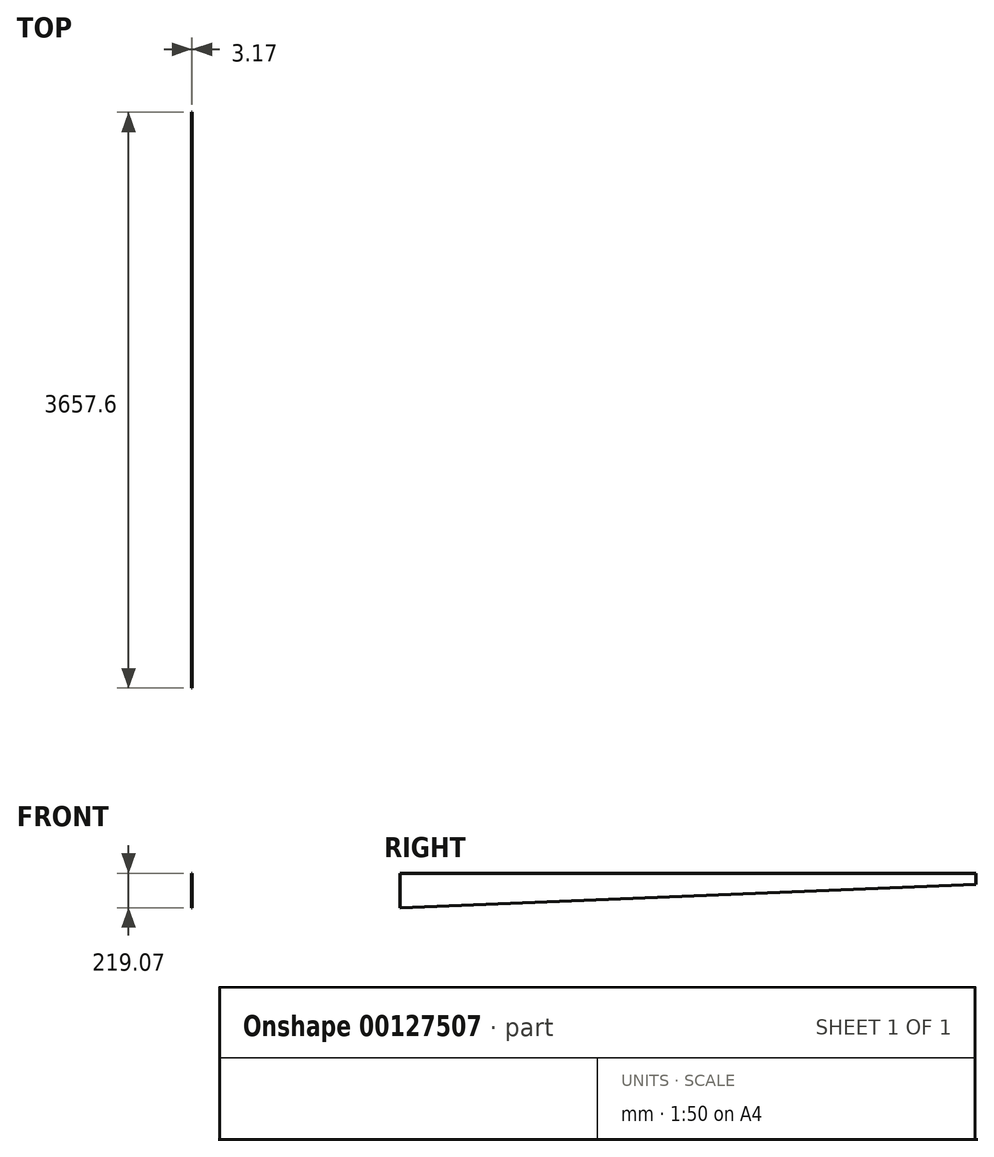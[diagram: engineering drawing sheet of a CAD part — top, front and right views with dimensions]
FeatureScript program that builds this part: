
annotation { "Feature Type Name" : "Feature", "Feature Type Description" : "" }
export const myFeature = defineFeature(function(context is Context, id is Id, definition is map)
    precondition{}
    {
        {
            var Q0;
            Q0=qCreatedBy(makeId("Right.planeOp"),FACE);
            var sketch = newSketch(context, id + "F0", { "sketchPlane" : qUnion([Q0])});
            skLineSegment(sketch, "E0", {"start": v(0, 0) * mm, "end": v(0, -219.08) * mm});
            skLineSegment(sketch, "E1", {"start": v(0, -219.08) * mm, "end": v(3657.6, -70.64) * mm});
            skLineSegment(sketch, "E2", {"start": v(3657.6, -70.64) * mm, "end": v(3657.6, 0) * mm});
            skLineSegment(sketch, "E3", {"start": v(3657.6, 0) * mm, "end": v(0, 0) * mm});
            skSolve(sketch);
        }
        {
            var Q0;
            Q0 = qSketchRegion(id + "F0", true);
            extrude(context, id + "F1", {"entities" : qUnion([Q0]), "depth" : 3.17 * mm});
        }
    });
